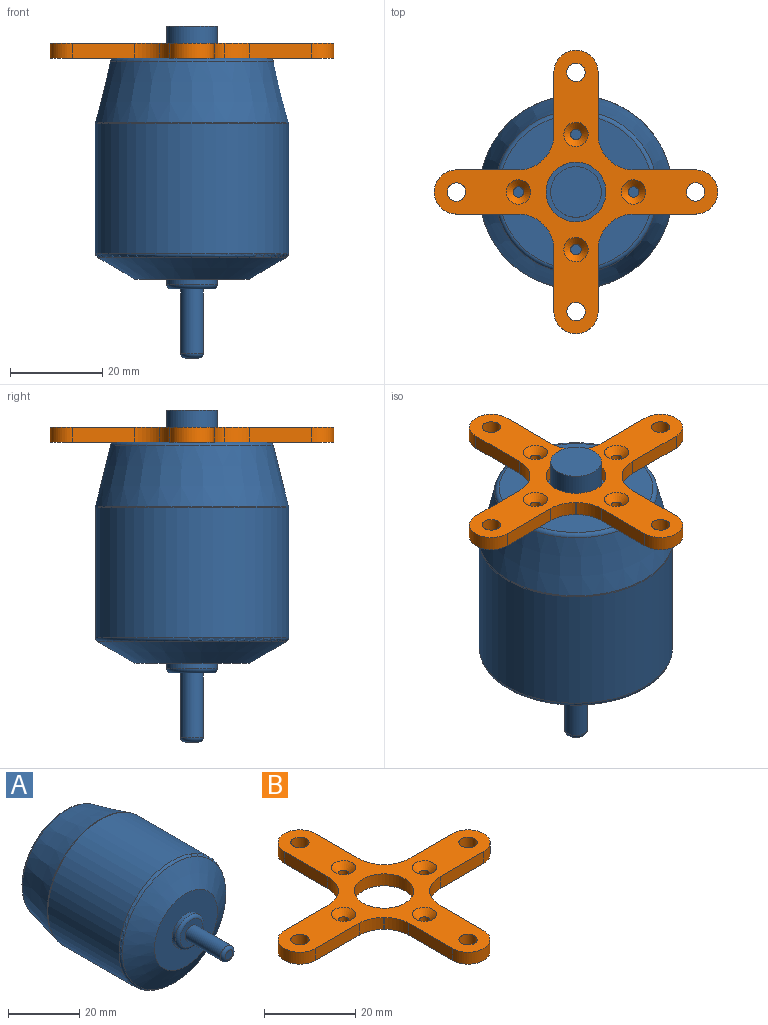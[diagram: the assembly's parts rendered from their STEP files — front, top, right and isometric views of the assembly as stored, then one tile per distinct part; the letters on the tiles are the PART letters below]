
ASSEMBLY  parts=2 mates=1
PART A: 24 faces, bbox 45.5x72.2x45.5 mm
  f0: plane 3x3mm, normal (0,-1,0), area 7.1mm2, adj f19
  f1: cylinder r=2.5mm len=14mm, axis (0,-1,0), area 219.9mm2, adj f2,f19
  f2: plane 9x9mm, normal (0,-1,0), area 44mm2, adj f1,f20
  f3: cylinder r=5.5mm len=11mm, axis (0,-1,0), area 39.7mm2, adj f4,f20
  f4: plane 25x25mm, normal (0,-1,0), area 395.8mm2, adj f3,f5
  f5: cone r=12.5mm half-angle=59.5deg, axis (0,1,0), area 963.3mm2, adj f4,f21
  f6: cylinder r=21mm len=42mm, axis (0,-1,0), area 3734.7mm2, adj f21,f22
  f7: cone r=21mm half-angle=14deg, axis (0,-1,0), area 1642.9mm2, adj f22,f23
  f8: plane 33.44x33.44mm, normal (0,1,0), area 766.5mm2, adj f9,f11,f13,f15,f17,f23
  f9: cylinder r=5.5mm len=11mm, axis (0,-1,0), area 241.9mm2, adj f8,f10
  f10: plane 11x11mm, normal (0,1,0), area 95mm2, adj f9
  f11: cylinder r=1.15mm len=5mm, axis (0,1,0), area 36.1mm2, adj f8,f12
  f12: plane 2.3x2.3mm, normal (0,1,0), area 4.2mm2, adj f11
  f13: cylinder r=1.15mm len=5mm, axis (0,1,0), area 36.1mm2, adj f8,f14
  f14: plane 2.3x2.3mm, normal (0,1,0), area 4.2mm2, adj f13
  f15: cylinder r=1.15mm len=5mm, axis (0,1,0), area 36.1mm2, adj f8,f16
  f16: plane 2.3x2.3mm, normal (0,1,0), area 4.2mm2, adj f15
  f17: cylinder r=1.15mm len=5mm, axis (0,1,0), area 36.1mm2, adj f8,f18
  f18: plane 2.3x2.3mm, normal (0,1,0), area 4.2mm2, adj f17
  f19: torus R=1.5mm, axis (0,-1,0), area 21.1mm2, adj f0,f1
  f20: torus R=4.5mm, axis (0,-1,0), area 50.7mm2, adj f2,f3
  f21: torus R=20mm, axis (0,1,0), area 136mm2, adj f5,f6
  f22: torus R=20mm, axis (0,1,0), area 32.3mm2, adj f6,f7
  f23: torus R=16.72mm, axis (0,-1,0), area 144mm2, adj f7,f8
PART B: 39 faces, bbox 61.6x61.6x3.2 mm
  f0: cylinder r=10mm len=3.2mm, axis (0,0,-1), area 0.1mm2, adj f12,f13,f23,f31
  f1: cylinder r=10mm len=3.2mm, axis (0,0,-1), area 0.1mm2, adj f12,f13,f20,f30
  f2: cylinder r=10mm len=3.2mm, axis (0,0,-1), area 0.1mm2, adj f5,f12,f13,f24
  f3: cylinder r=4.8mm len=9.6mm, axis (0,0,-1), area 48.3mm2, adj f4,f9,f12,f13
  f4: plane 13.47x3.2mm, normal (-1,0,0), area 43.1mm2, adj f3,f5,f12,f13
  f5: cylinder r=7.69mm len=5.44mm, axis (0,0,-1), area 19.4mm2, adj f2,f4,f12,f13
  f6: cylinder r=10mm len=3.2mm, axis (0,0,-1), area 0.1mm2, adj f7,f12,f13,f19
  f7: cylinder r=7.69mm len=5.44mm, axis (0,0,-1), area 19.4mm2, adj f6,f9,f12,f13
  f8: cylinder r=1.15mm len=2.3mm, axis (0,0,-1), area 12.3mm2, adj f13,f38
  f9: plane 13.47x3.2mm, normal (1,0,0), area 43.1mm2, adj f3,f7,f12,f13
  f10: cylinder r=2mm len=4mm, axis (0,0,-1), area 40.2mm2, adj f12,f13
  f11: cylinder r=6.5mm len=13mm, axis (0,0,-1), area 130.7mm2, adj f12,f13
  f12: plane 61.6x61.6mm, normal (0,0,1), area 831.2mm2, adj f0,f1,f2,f3,f4,f5,f6,f7
  f13: plane 61.6x61.6mm, normal (0,0,-1), area 902.8mm2, adj f0,f1,f2,f3,f4,f5,f6,f7
  f14: plane 13.47x3.2mm, normal (0,-1,0), area 43.1mm2, adj f12,f13,f15,f20
  f15: cylinder r=4.8mm len=9.6mm, axis (0,0,-1), area 48.3mm2, adj f12,f13,f14,f16
  f16: plane 13.47x3.2mm, normal (0,1,0), area 43.1mm2, adj f12,f13,f15,f19
  f17: cylinder r=1.15mm len=2.3mm, axis (0,0,-1), area 12.3mm2, adj f13,f37
  f18: cylinder r=2mm len=4mm, axis (0,0,-1), area 40.2mm2, adj f12,f13
  f19: cylinder r=7.69mm len=5.44mm, axis (0,0,-1), area 19.4mm2, adj f6,f12,f13,f16
  f20: cylinder r=7.69mm len=5.44mm, axis (0,0,-1), area 19.4mm2, adj f1,f12,f13,f14
  f21: cylinder r=4.8mm len=9.6mm, axis (0,0,-1), area 48.3mm2, adj f12,f13,f22,f26
  f22: plane 13.47x3.2mm, normal (0,-1,0), area 43.1mm2, adj f12,f13,f21,f23
  f23: cylinder r=7.69mm len=5.44mm, axis (0,0,-1), area 19.4mm2, adj f0,f12,f13,f22
  f24: cylinder r=7.69mm len=5.44mm, axis (0,0,-1), area 19.4mm2, adj f2,f12,f13,f26
  f25: cylinder r=1.15mm len=2.3mm, axis (0,0,-1), area 12.3mm2, adj f13,f35
  f26: plane 13.47x3.2mm, normal (0,1,0), area 43.1mm2, adj f12,f13,f21,f24
  f27: cylinder r=2mm len=4mm, axis (0,0,-1), area 40.2mm2, adj f12,f13
  f28: cylinder r=4.8mm len=9.6mm, axis (0,0,-1), area 48.3mm2, adj f12,f13,f29,f33
  f29: plane 13.47x3.2mm, normal (1,0,0), area 43.1mm2, adj f12,f13,f28,f30
  f30: cylinder r=7.69mm len=5.44mm, axis (0,0,-1), area 19.4mm2, adj f1,f12,f13,f29
  f31: cylinder r=7.69mm len=5.44mm, axis (0,0,-1), area 19.4mm2, adj f0,f12,f13,f33
  f32: cylinder r=1.15mm len=2.3mm, axis (0,0,-1), area 12.3mm2, adj f13,f36
  f33: plane 13.47x3.2mm, normal (-1,0,0), area 43.1mm2, adj f12,f13,f28,f31
  f34: cylinder r=2mm len=4mm, axis (0,0,-1), area 40.2mm2, adj f12,f13
  f35: cone r=2.65mm half-angle=45deg, axis (0,0,1), area 25.3mm2, adj f12,f25
  f36: cone r=2.65mm half-angle=45deg, axis (0,0,1), area 25.3mm2, adj f12,f32
  f37: cone r=2.65mm half-angle=45deg, axis (0,0,1), area 25.3mm2, adj f12,f17
  f38: cone r=2.65mm half-angle=45deg, axis (0,0,1), area 25.3mm2, adj f8,f12
PLACE A rot(axis=(1,0,0),90deg) t=(0,0,-72.15)mm fixed
PLACE B t=(0,0,-7)mm
MATE fastened A.f1 <-> B.f11  axis (0,0,-1) through (0,0,-7)mm
